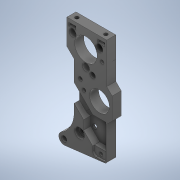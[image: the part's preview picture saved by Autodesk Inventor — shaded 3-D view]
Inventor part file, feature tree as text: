
AUTODESK INVENTOR PART (.ipt)
format: ipt  version: 2020 (Build 240168000, 168)  size: 562,176 bytes
history: native  units: mm
features: extrude x14, sketch x10, fillet x5, projected_geometry x5, thread x2, chamfer x1
ambient origin geometry x8: Origin, YZ Plane, XZ Plane, XY Plane, X Axis, Y Axis, Z Axis, Center Point
bodies: Solid1 (feature_tree)
feature tree (37):
  extrude  "Extrusion1"  Depth=23.5mm
  fillet  "Fillet1"  Radius=23.5mm
  fillet  "Fillet2"  Radius=6.0mm
  extrude  "Extrusion2"  Depth=3.0mm
  extrude  "Extrusion3"  Depth=4.0mm
  thread  "Thread1"  [1 undecoded]
  thread  "Thread2"  [1 undecoded]
  extrude  "Extrusion4"  Depth=24.75mm
  extrude  "Extrusion5"  Depth=2.1mm
  extrude  "Extrusion6"  Depth=4.0mm
  extrude  "Extrusion7"  TaperAngle=45.0deg  [1 undecoded]
  extrude  "Extrusion8"  Depth=12.0mm
  extrude  "Extrusion9"  TaperAngle=135.0deg  [1 undecoded]
  extrude  "Extrusion10"  Depth=5.0mm TaperAngle=0.0deg
  fillet  "Fillet3"  Radius=3.0mm
  extrude  "Extrusion11"  Depth=10.0mm
  chamfer  "Chamfer1"  Distance=3.0mm
  fillet  "Fillet4"  Radius=2.5mm
  extrude  "Extrusion12"  Depth=0.5mm
  extrude  "Extrusion13"  Depth=7.5mm
  extrude  "Extrusion14"  Depth=0.5mm
  fillet  "Fillet5"  Radius=15.0mm
  sketch  "Sketch3"  dims[d0=3.0mm d1=6.0mm d2=23.5mm d3=6.0mm]
  projected_geometry  "Projected Loop1"
  sketch  "Sketch5"  dims[d4=0.0mm d5=3.0mm]
  sketch  "Sketch7"  dims[d6=18.0mm d7=56.0mm d8=11.0mm d9=4.0mm]
  sketch  "Sketch8"  dims[d10=24.75mm d11=12.5mm]
  projected_geometry  "Projected Loop2"
  sketch  "Sketch10"  dims[d12=22.3mm d14=2.1mm]
  sketch  "Sketch13"  dims[d18=30.0mm d20=360.0deg d22=4.0mm]
  sketch  "Sketch15"  dims[d23=14.0mm d24=45.0deg]
  sketch  "Sketch17"  dims[d25=3.0mm d26=12.0mm]
  projected_geometry  "Projected Loop3"
  sketch  "Sketch21"  dims[d27=6.0mm d28=135.0deg]
  projected_geometry  "Projected Loop5"
  sketch  "Sketch22"  dims[d29=135.0deg d30=5.0mm d31=0.0mm d32=3.0mm d33=10.0mm d34=3.0mm d35=2.5mm d36=13.5mm d37=7.5mm d38=2.5mm d39=15.0mm d40=12.5mm d41=1.0mm d42=15.0mm d43=12.75mm d44=20.0mm d45=23.75mm d46=3.0mm d47=0.0mm d48=2.0mm d49=2.0mm d50=2.5mm d51=2.5mm d52=3.0mm d53=3.0mm d54=4.5mm d55=0.0mm d56=7.0mm d57=0.0mm d58=7.0mm d59=0.0mm d60=8.5mm d61=270.0deg d62=4.0mm d63=4.0mm d64=4.0mm d65=3.0mm d66=0.0mm d67=5.5mm d68=2.0mm d69=0.0mm d70=4.0mm d71=1.85mm d72=4.0mm d73=1.85mm d74=1.0mm d75=2.8mm d76=2.8mm d77=1.0mm d78=10.0mm d79=0.0mm d82=3.1mm d83=11.15mm d84=2.1mm d85=2.1mm d86=2.1mm d87=5.5mm d88=3.5mm d89=25.75mm d90=30.25mm d91=2.5mm d92=11.75mm d93=24.0mm d94=8.0mm d95=2.1mm d96=2.1mm d98=2.1mm d99=1.8mm d100=0.0mm d101=2.1mm d102=2.1mm d103=2.1mm d104=1.8mm d105=0.0mm d117=3.9mm d118=0.0mm d119=18.0mm d120=6.5mm d121=0.0mm d122=1.0mm d125=5.0mm d126=7.25mm d127=2.5mm d128=5.0mm d129=15.0mm d130=5.0mm d131=5.0mm d132=90.0deg d133=135.0deg d135=135.0deg d136=135.0deg d137=3.0mm d138=0.0mm d139=0.9mm d140=2.0mm d141=45.0deg d142=4.0mm d143=2.0mm d144=2.6mm d145=3.625mm d146=10.0mm d147=0.0mm d148=2.05mm d149=2.4mm d150=0.0mm d151=4.5mm d154=1.0mm d155=0.0mm d156=2.0mm d157=2.8mm d80=0.5mm d81=0.872665mm d106=0.872665mm d123=0.872665mm d134=0.5mm d153=0.5mm]
  projected_geometry  "Projected Loop6"
note: 4 required parameter values undecoded (feature->parameter linkage not recoverable at this tier; creation-order binding heuristic only, values carry confidence <= 0.55)
